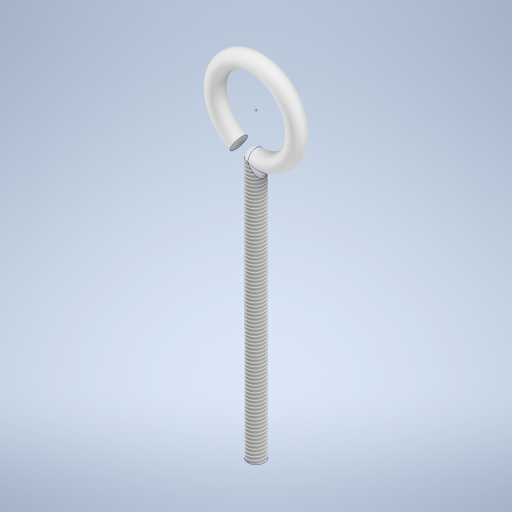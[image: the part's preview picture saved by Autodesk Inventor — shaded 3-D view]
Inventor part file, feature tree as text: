
AUTODESK INVENTOR PART (.ipt)
format: ipt  version: 2024 (Build 280153000, 153)  size: 308,224 bytes
history: native  units: in
note: dims shown in document units (in); Inventor stores cm internally (conversion verified against a paired STEP export)
features: sketch x3, revolve x2, extrude x1, fillet x1, thread x1, other x1, projected_geometry x1
ambient origin geometry x8: Origin, YZ Plane, XZ Plane, XY Plane, X Axis, Y Axis, Z Axis, Center Point
bodies: Solid1 (feature_tree)
feature tree (10):
  revolve  "Revolution1"  [1 undecoded]
  extrude  "Extrusion1"  Depth=4.0in TaperAngle=0.0deg
  revolve  "Revolution2"  [1 undecoded]
  fillet  "Fillet1"  Radius=4.0in
  thread  "Thread1"  [1 undecoded]
  other  "Work Point1"
  sketch  "Sketch1"  dims[d0=0.25in d1=0.5in]
  sketch  "Sketch2"  dims[d2=2.3019in d3=4.0in d4=0.0in]
  sketch  "Sketch3"  dims[d5=360.0deg d6=0.125in d7=4.0in d8=0.0in]
  projected_geometry  "Projected Loop1"
note: 3 required parameter values undecoded (feature->parameter linkage not recoverable at this tier; creation-order binding heuristic only, values carry confidence <= 0.55)